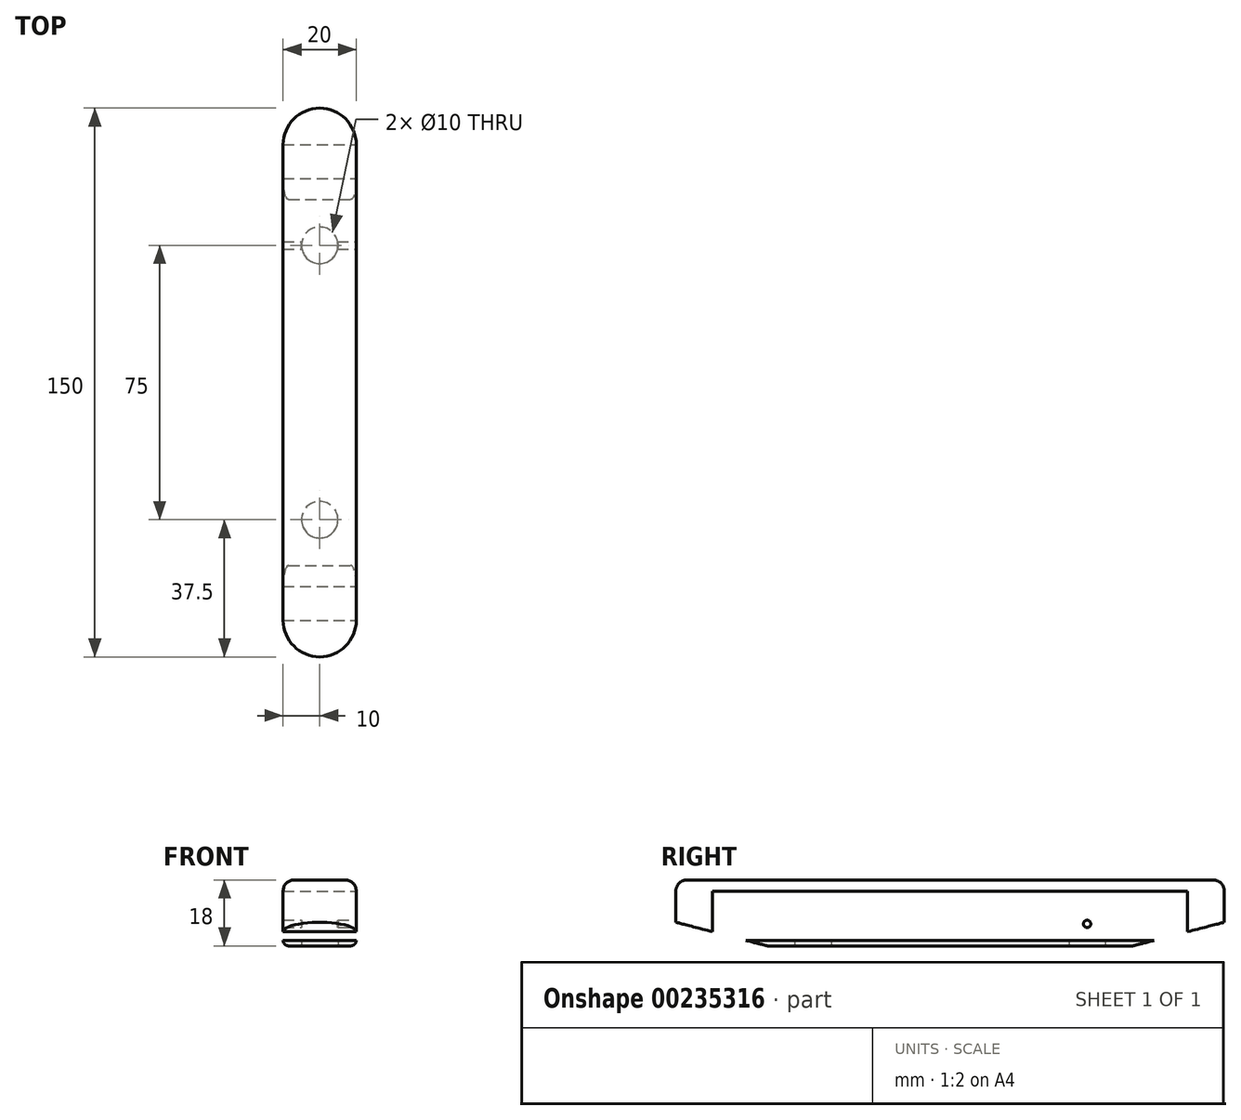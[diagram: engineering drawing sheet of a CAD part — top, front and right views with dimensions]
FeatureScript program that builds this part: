
annotation { "Feature Type Name" : "Feature", "Feature Type Description" : "" }
export const myFeature = defineFeature(function(context is Context, id is Id, definition is map)
    precondition{}
    {
        {
            var Q0;
            Q0=qCreatedBy(makeId("Top.planeOp"),FACE);
            var sketch = newSketch(context, id + "F0", { "sketchPlane" : qUnion([Q0])});
            skLineSegment(sketch, "E0.bottom", {"start": v(0, -75) * mm, "end": v(0, -75) * mm});
            skLineSegment(sketch, "E0.top", {"start": v(0, 75) * mm, "end": v(0, 75) * mm});
            skLineSegment(sketch, "E0.left", {"start": v(10, -65) * mm, "end": v(10, 65) * mm});
            skLineSegment(sketch, "E0.right", {"start": v(-10, -65) * mm, "end": v(-10, 65) * mm});
            skPoint(sketch, "E0.middle", {"position": v(0, 0) * mm});
            skCircle(sketch, "E1", {"center": v(0, -37.5) * mm, "radius": 5 * mm});
            skCircle(sketch, "E2", {"center": v(0, 37.5) * mm, "radius": 5 * mm});
            skPoint(sketch, "E3.visualSharp", {"position": v(-10, 75) * mm});
            skArc(sketch, "E3.filletArc", {"start": v(0, 75) * mm, "mid": v(-7.07, 72.07) * mm, "end": v(-10, 65) * mm});
            skPoint(sketch, "E4.visualSharp", {"position": v(10, 75) * mm});
            skArc(sketch, "E4.filletArc", {"start": v(10, 65) * mm, "mid": v(7.07, 72.07) * mm, "end": v(0, 75) * mm});
            skPoint(sketch, "E5.visualSharp", {"position": v(10, -75) * mm});
            skArc(sketch, "E5.filletArc", {"start": v(0, -75) * mm, "mid": v(7.07, -72.07) * mm, "end": v(10, -65) * mm});
            skPoint(sketch, "E6.visualSharp", {"position": v(-10, -75) * mm});
            skArc(sketch, "E6.filletArc", {"start": v(-10, -65) * mm, "mid": v(-7.07, -72.07) * mm, "end": v(0, -75) * mm});
            skSolve(sketch);
        }
        {
            var Q0;
            Q0=makeQuery(id+"F0.imprint","IMPRINT",FACE,{"disambiguationData":[TD([[makeQuery(id+"F0.imprint","IMPRINT",EDGE,{"derivedFrom":sQuery(id+"F0.wireOp",EDGE,"E0.left")}),1.0]])]});
            var Q1;
            Q1=makeQuery(id+"F0.imprint","IMPRINT",FACE,{"disambiguationData":[TD([[makeQuery(id+"F0.imprint","IMPRINT",EDGE,{"derivedFrom":sQuery(id+"F0.wireOp",EDGE,"E1")}),1.0]])]});
            var Q2;
            Q2=makeQuery(id+"F0.imprint","IMPRINT",FACE,{"disambiguationData":[TD([[makeQuery(id+"F0.imprint","IMPRINT",EDGE,{"derivedFrom":sQuery(id+"F0.wireOp",EDGE,"E2")}),1.0]])]});
            extrude(context, id + "F1", {"entities" : qUnion([Q0, Q1, Q2]), "depth" : 18 * mm});
        }
        {
            var Q0;
            Q0=makeQuery(id+"F0.imprint","IMPRINT",FACE,{"disambiguationData":[TD([[makeQuery(id+"F0.imprint","IMPRINT",EDGE,{"derivedFrom":sQuery(id+"F0.wireOp",EDGE,"E1")}),1.0]])]});
            var Q1;
            Q1=makeQuery(id+"F0.imprint","IMPRINT",FACE,{"disambiguationData":[TD([[makeQuery(id+"F0.imprint","IMPRINT",EDGE,{"derivedFrom":sQuery(id+"F0.wireOp",EDGE,"E2")}),1.0]])]});
            extrude(context, id + "F2", {"entities" : qUnion([Q0, Q1]), "operationType" : NewBodyOperationType.REMOVE, "depth" : 10 * mm});
        }
        {
            var Q0;
            Q0=makeQuery(id+"F1.opExtrude","SWEPT_FACE",FACE,{"disambiguationData":[OSD([sQuery(id+"F0.wireOp",EDGE,"E0.left")])]});
            var sketch = newSketch(context, id + "F3", { "sketchPlane" : qUnion([Q0])});
            skLineSegment(sketch, "E7", {"start": v(-50, 0) * mm, "end": v(-88.73, 10) * mm});
            skLineSegment(sketch, "E8", {"start": v(-88.73, 10) * mm, "end": v(-88.73, 0) * mm});
            skLineSegment(sketch, "E9", {"start": v(-88.73, 0) * mm, "end": v(-50, 0) * mm});
            skLineSegment(sketch, "E10", {"start": v(0, 0) * mm, "end": v(0, 18) * mm});
            skLineSegment(sketch, "E11.MirrorCS", {"start": v(88.73, 10) * mm, "end": v(88.73, 0) * mm});
            skLineSegment(sketch, "E12.MirrorCS", {"start": v(88.73, 0) * mm, "end": v(50, 0) * mm});
            skLineSegment(sketch, "E13.MirrorCS", {"start": v(50, 0) * mm, "end": v(88.73, 10) * mm});
            skSolve(sketch);
        }
        {
            var Q0;
            {var subQ0=sQuery(id+"F3.wireOp",EDGE,"E8");Q0=makeQuery(id+"F3.imprint","IMPRINT",FACE,{"disambiguationData":[TD([[makeQuery(id+"F3.imprint","IMPRINT",EDGE,{"derivedFrom":subQ0}),1.0]])]});}
            var Q1;
            {var subQ0=sQuery(id+"F3.wireOp",EDGE,"E9");var subQ1=sQuery(id+"F3.wireOp",EDGE,"E7");var subQ2=sQuery(id+"F0.wireOp",EDGE,"E0.left");var subQ3=makeQuery(id+"F3.imprint","INTERSECT",VERTEX,{"derivedFrom":[makeQuery(id+"F1.opExtrude","CAP_EDGE",EDGE,{"disambiguationData":[OSD([subQ2])],"isStart":true}),subQ1,subQ0]});Q1=makeQuery(id+"F3.imprint","IMPRINT",FACE,{"disambiguationData":[TD([[makeQuery(id+"F3.imprint","IMPRINT",EDGE,{"disambiguationData":[TD([[subQ3,-1.0]])],"derivedFrom":subQ1}),1.0]])]});}
            var Q2;
            {var subQ0=sQuery(id+"F3.wireOp",EDGE,"E11.MirrorCS");Q2=makeQuery(id+"F3.imprint","IMPRINT",FACE,{"disambiguationData":[TD([[makeQuery(id+"F3.imprint","IMPRINT",EDGE,{"derivedFrom":subQ0}),-1.0]])]});}
            var Q3;
            {var subQ0=sQuery(id+"F3.wireOp",EDGE,"E12.MirrorCS");var subQ1=sQuery(id+"F0.wireOp",EDGE,"E0.left");var subQ4=sQuery(id+"F3.wireOp",EDGE,"E13.MirrorCS");var subQ5=makeQuery(id+"F3.imprint","INTERSECT",VERTEX,{"derivedFrom":[makeQuery(id+"F1.opExtrude","CAP_EDGE",EDGE,{"disambiguationData":[OSD([subQ1])],"isStart":true}),subQ0,subQ4]});Q3=makeQuery(id+"F3.imprint","IMPRINT",FACE,{"disambiguationData":[TD([[makeQuery(id+"F3.imprint","IMPRINT",EDGE,{"disambiguationData":[TD([[subQ5,-1.0]])],"derivedFrom":subQ0}),1.0]])]});}
            extrude(context, id + "F4", {"entities" : qUnion([Q0, Q1, Q2, Q3]), "operationType" : NewBodyOperationType.REMOVE, "endBound" : BoundingType.THROUGH_ALL, "oppositeDirection" : true, "depth" : 25 * mm});
        }
        {
            var Q0;
            Q0=makeQuery(id+"F4.boolean.opBoolean","COPY",EDGE,{"derivedFrom":makeQuery(id+"F4.opExtrude","CAP_EDGE",EDGE,{"disambiguationData":[OSD([sQuery(id+"F3.wireOp",EDGE,"E7")])],"isStart":true})});
            var Q1;
            Q1=makeQuery(id+"F4.boolean.opBoolean","COPY",EDGE,{"derivedFrom":makeQuery(id+"F4.opExtrude","CAP_EDGE",EDGE,{"disambiguationData":[OSD([sQuery(id+"F3.wireOp",EDGE,"E13.MirrorCS")])],"isStart":true})});
            var Q2;
            Q2=makeQuery(id+"F1.opExtrude","CAP_EDGE",EDGE,{"disambiguationData":[OSD([sQuery(id+"F0.wireOp",EDGE,"E0.left")])],"isStart":true});
            var Q3;
            Q3=makeQuery(id+"F1.opExtrude","CAP_EDGE",EDGE,{"disambiguationData":[OSD([sQuery(id+"F0.wireOp",EDGE,"E0.right")])],"isStart":true});
            fillet(context, id + "F5", {"entities" : qUnion([Q0, Q1, Q2, Q3]), "radius" : 1.5 * mm, "tangentPropagation" : true, "allowEdgeOverflow" : false});
        }
        {
            var Q0;
            Q0=makeQuery(id+"F1.opExtrude","CAP_EDGE",EDGE,{"disambiguationData":[OSD([sQuery(id+"F0.wireOp",EDGE,"E0.right")])],"isStart":false});
            fillet(context, id + "F6", {"entities" : qUnion([Q0]), "radius" : 3 * mm, "tangentPropagation" : true, "allowEdgeOverflow" : false});
        }
        {
            var Q0;
            Q0=makeQuery(id+"F1.opExtrude","SWEPT_FACE",FACE,{"disambiguationData":[OSD([sQuery(id+"F0.wireOp",EDGE,"E0.left")])]});
            var sketch = newSketch(context, id + "F7", { "sketchPlane" : qUnion([Q0])});
            skCircle(sketch, "E14", {"center": v(-37.5, 6) * mm, "radius": 1 * mm});
            skLineSegment(sketch, "E15", {"start": v(0, -2.45) * mm, "end": v(0, 22.55) * mm, "construction": true});
            skCircle(sketch, "E16.MirrorC", {"center": v(37.5, 6) * mm, "radius": 1 * mm});
            skSolve(sketch);
        }
        {
            var Q0;
            Q0=makeQuery(id+"F7.imprint","IMPRINT",FACE,{"disambiguationData":[TD([[makeQuery(id+"F7.imprint","IMPRINT",EDGE,{"derivedFrom":sQuery(id+"F7.wireOp",EDGE,"E14")}),1.0]])]});
            var Q1;
            Q1=makeQuery(id+"F7.imprint","IMPRINT",FACE,{"disambiguationData":[TD([[makeQuery(id+"F7.imprint","IMPRINT",EDGE,{"derivedFrom":sQuery(id+"F7.wireOp",EDGE,"E16.MirrorC")}),-1.0]])]});
            var Q2;
            Q2=sQuery(id+"F7.wireOp",EDGE,"E14");
            var Q3;
            Q3=sQuery(id+"F7.wireOp",EDGE,"E16.MirrorC");
            extrude(context, id + "F8", {"entities" : qUnion([Q0, Q1]), "operationType" : NewBodyOperationType.REMOVE, "surfaceEntities" : qUnion([Q2, Q3]), "endBound" : BoundingType.THROUGH_ALL, "oppositeDirection" : true, "depth" : 25 * mm});
        }
    });
